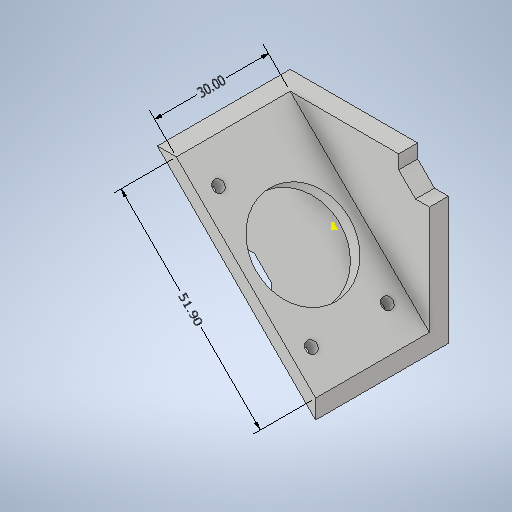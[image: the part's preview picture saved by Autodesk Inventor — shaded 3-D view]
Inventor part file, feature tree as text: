
AUTODESK INVENTOR PART (.ipt)
format: ipt  version: 2025 (Build 290162000, 162)  size: 316,416 bytes
history: native  units: mm
features: sketch x7, extrude x3, hole x3, other x2
ambient origin geometry x8: Origin, YZ Plane, XZ Plane, XY Plane, X Axis, Y Axis, Z Axis, Center Point
bodies: 实体1 (feature_tree)
feature tree (15):
  extrude  "拉伸1"  Depth=30.0mm TaperAngle=0.0deg
  sketch  "草图2"  dims[d12=24.5mm d13=6.0mm d14=4.0mm d15=2.0mm d16=90.0deg d17=8.0mm d18=20.594885mm]
  extrude  "拉伸2"  Depth=30.0mm TaperAngle=0.0deg
  hole  "孔1"  [1 undecoded]
  hole  "孔2"  [1 undecoded]
  extrude  "拉伸3"  Depth=1.0mm
  hole  "孔3"  [1 undecoded]
  sketch  "草图1"  dims[d8=5.0mm d9=0.0mm d10=30.0mm d11=0.0mm]
  sketch  "草图3"  dims[d19=0.01mm d20=6.0mm d21=4.0mm d22=2.0mm d23=90.0deg d24=8.0mm d25=20.594885mm d26=30.0mm d27=0.0mm]
  sketch  "草图4"  dims[d36=2.97mm d37=6.0mm d38=4.0mm d39=2.0mm d40=90.0deg d41=0.5mm d42=20.594885mm]
  sketch  "草图5"  dims[d28=6.575673mm d29=8.362671mm d30=51.90253mm d31=8.575597mm d32=30.0mm d33=1.0mm]
  sketch  "草图6"  dims[d34=1.0mm d35=1.0mm]
  sketch  "草图7"  dims[d43=0.75mm d44=0.375mm]
  other  "线性尺寸 1"
  other  "线性尺寸 2"
note: 3 required parameter values undecoded (feature->parameter linkage not recoverable at this tier; creation-order binding heuristic only, values carry confidence <= 0.55)
